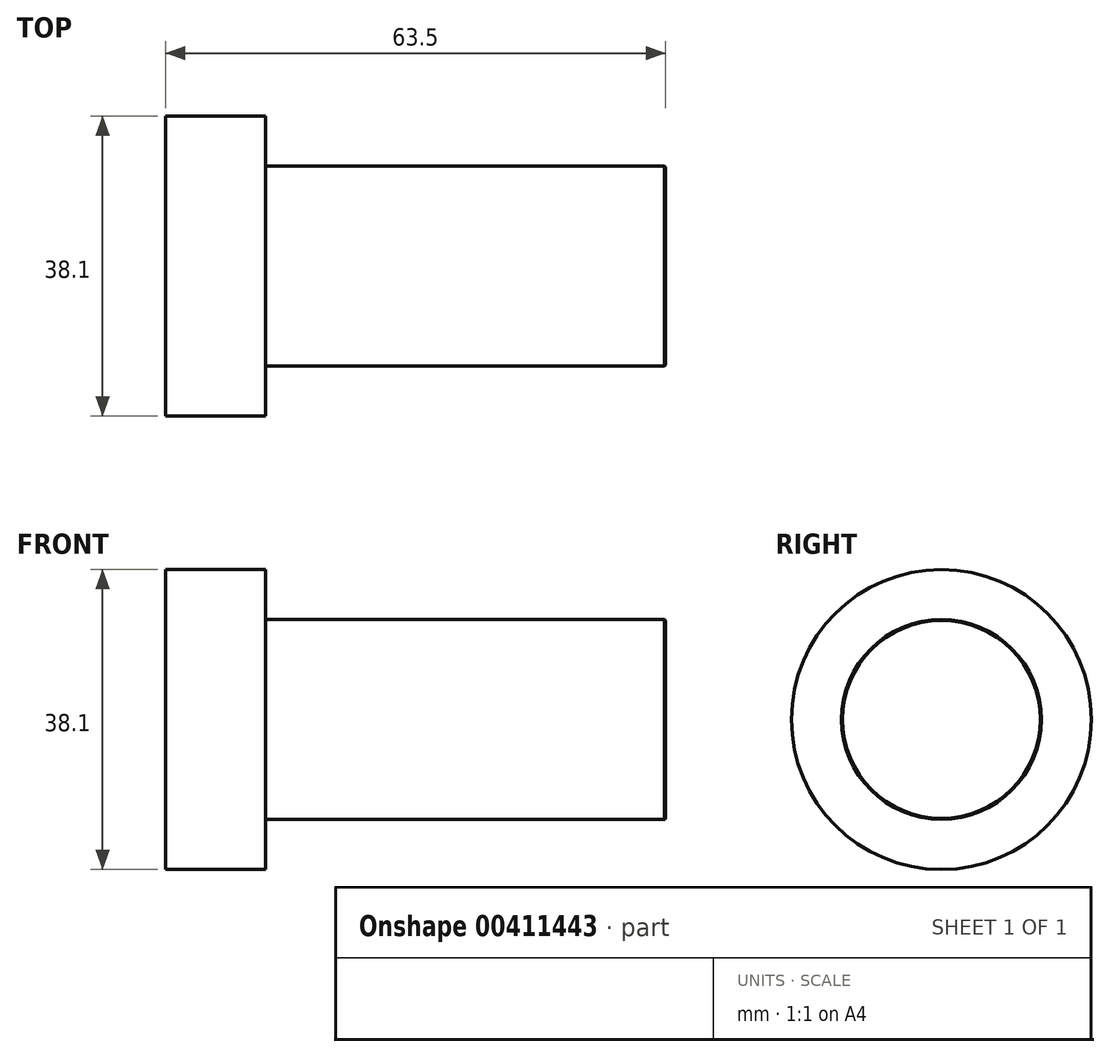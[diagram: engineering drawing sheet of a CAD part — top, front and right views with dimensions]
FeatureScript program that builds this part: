
annotation { "Feature Type Name" : "Feature", "Feature Type Description" : "" }
export const myFeature = defineFeature(function(context is Context, id is Id, definition is map)
    precondition{}
    {
        {
            var Q0;
            Q0=qCreatedBy(makeId("Right.planeOp"),FACE);
            var sketch = newSketch(context, id + "F0", { "sketchPlane" : qUnion([Q0])});
            skCircle(sketch, "E0", {"center": v(0, 0) * mm, "radius": 19.05 * mm});
            skSolve(sketch);
        }
        {
            var Q0;
            Q0=makeQuery(id+"F0.imprint","IMPRINT",FACE,{"disambiguationData":[TD([[makeQuery(id+"F0.imprint","IMPRINT",EDGE,{"derivedFrom":sQuery(id+"F0.wireOp",EDGE,"E0")}),1.0]])]});
            extrude(context, id + "F1", {"entities" : qUnion([Q0]), "oppositeDirection" : true, "depth" : 12.7 * mm});
        }
        {
            var Q0;
            Q0=makeQuery(id+"F1.opExtrude","CAP_FACE",FACE,{"disambiguationData":[OSD([sQuery(id+"F0.wireOp",EDGE,"E0")])],"isStart":true});
            var sketch = newSketch(context, id + "F2", { "sketchPlane" : qUnion([Q0])});
            skCircle(sketch, "E1", {"center": v(0, 0) * mm, "radius": 12.7 * mm});
            skSolve(sketch);
        }
        {
            var Q0;
            Q0 = qSketchRegion(id + "F2", true);
            extrude(context, id + "F3", {"entities" : qUnion([Q0]), "operationType" : NewBodyOperationType.ADD, "depth" : 50.8 * mm});
        }
        {
            var Q0;
            Q0=makeQuery(id+"F3.opExtrude","CAP_EDGE",EDGE,{"disambiguationData":[OSD([sQuery(id+"F2.wireOp",EDGE,"E1")])],"isStart":false});
            chamfer(context, id + "F4", {"entities" : qUnion([Q0]), "width" : 0.13 * mm, "tangentPropagation" : true});
        }
    });
